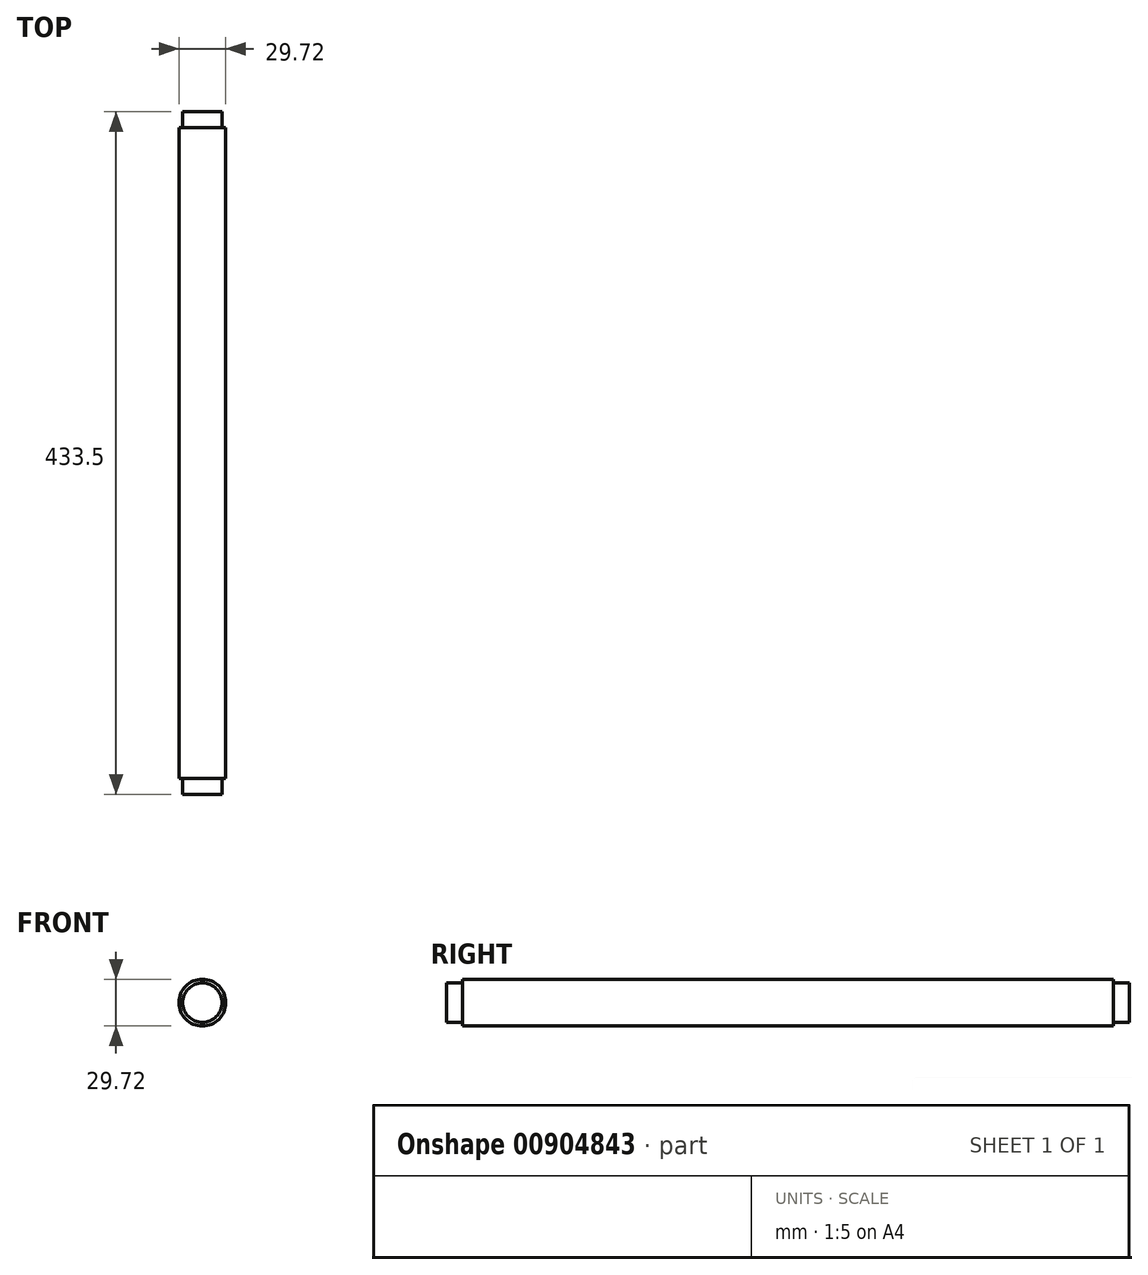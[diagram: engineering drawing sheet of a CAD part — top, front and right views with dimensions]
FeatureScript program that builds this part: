
annotation { "Feature Type Name" : "Feature", "Feature Type Description" : "" }
export const myFeature = defineFeature(function(context is Context, id is Id, definition is map)
    precondition{}
    {
        {
            var Q0;
            Q0=qCreatedBy(makeId("Front.planeOp"),FACE);
            var sketch = newSketch(context, id + "F0", { "sketchPlane" : qUnion([Q0])});
            skCircle(sketch, "E0", {"center": v(0, 0) * mm, "radius": 14.86 * mm});
            skSolve(sketch);
        }
        {
            var Q0;
            Q0=makeQuery(id+"F0.imprint","IMPRINT",FACE,{"disambiguationData":[TD([[makeQuery(id+"F0.imprint","IMPRINT",EDGE,{"derivedFrom":sQuery(id+"F0.wireOp",EDGE,"E0")}),1.0]])]});
            extrude(context, id + "F1", {"entities" : qUnion([Q0]), "depth" : 433.5 * mm, "offsetDistance" : 25 * mm});
        }
        {
            var Q0;
            Q0=makeQuery(id+"F1.opExtrude","CAP_FACE",FACE,{"disambiguationData":[OSD([sQuery(id+"F0.wireOp",EDGE,"E0")])],"isStart":true});
            var sketch = newSketch(context, id + "F2", { "sketchPlane" : qUnion([Q0])});
            skCircle(sketch, "E1", {"center": v(0, 0) * mm, "radius": 12.5 * mm});
            skSolve(sketch);
        }
        {
            var Q0;
            Q0=makeQuery(id+"F2.imprint","IMPRINT",FACE,{"disambiguationData":[TD([[makeQuery(id+"F2.imprint","IMPRINT",EDGE,{"derivedFrom":sQuery(id+"F2.wireOp",EDGE,"E1")}),-1.0]])]});
            extrude(context, id + "F3", {"entities" : qUnion([Q0]), "operationType" : NewBodyOperationType.REMOVE, "oppositeDirection" : true, "depth" : 10 * mm, "offsetDistance" : 25 * mm});
        }
        {
            var Q0;
            Q0=makeQuery(id+"F1.opExtrude","CAP_FACE",FACE,{"disambiguationData":[OSD([sQuery(id+"F0.wireOp",EDGE,"E0")])],"isStart":false});
            var sketch = newSketch(context, id + "F4", { "sketchPlane" : qUnion([Q0])});
            skCircle(sketch, "E2", {"center": v(0, 0) * mm, "radius": 12.5 * mm});
            skSolve(sketch);
        }
        {
            var Q0;
            Q0=makeQuery(id+"F4.imprint","IMPRINT",FACE,{"disambiguationData":[TD([[makeQuery(id+"F4.imprint","IMPRINT",EDGE,{"derivedFrom":sQuery(id+"F4.wireOp",EDGE,"E2")}),-1.0]])]});
            extrude(context, id + "F5", {"entities" : qUnion([Q0]), "operationType" : NewBodyOperationType.REMOVE, "oppositeDirection" : true, "depth" : 10 * mm, "offsetDistance" : 25 * mm});
        }
    });
